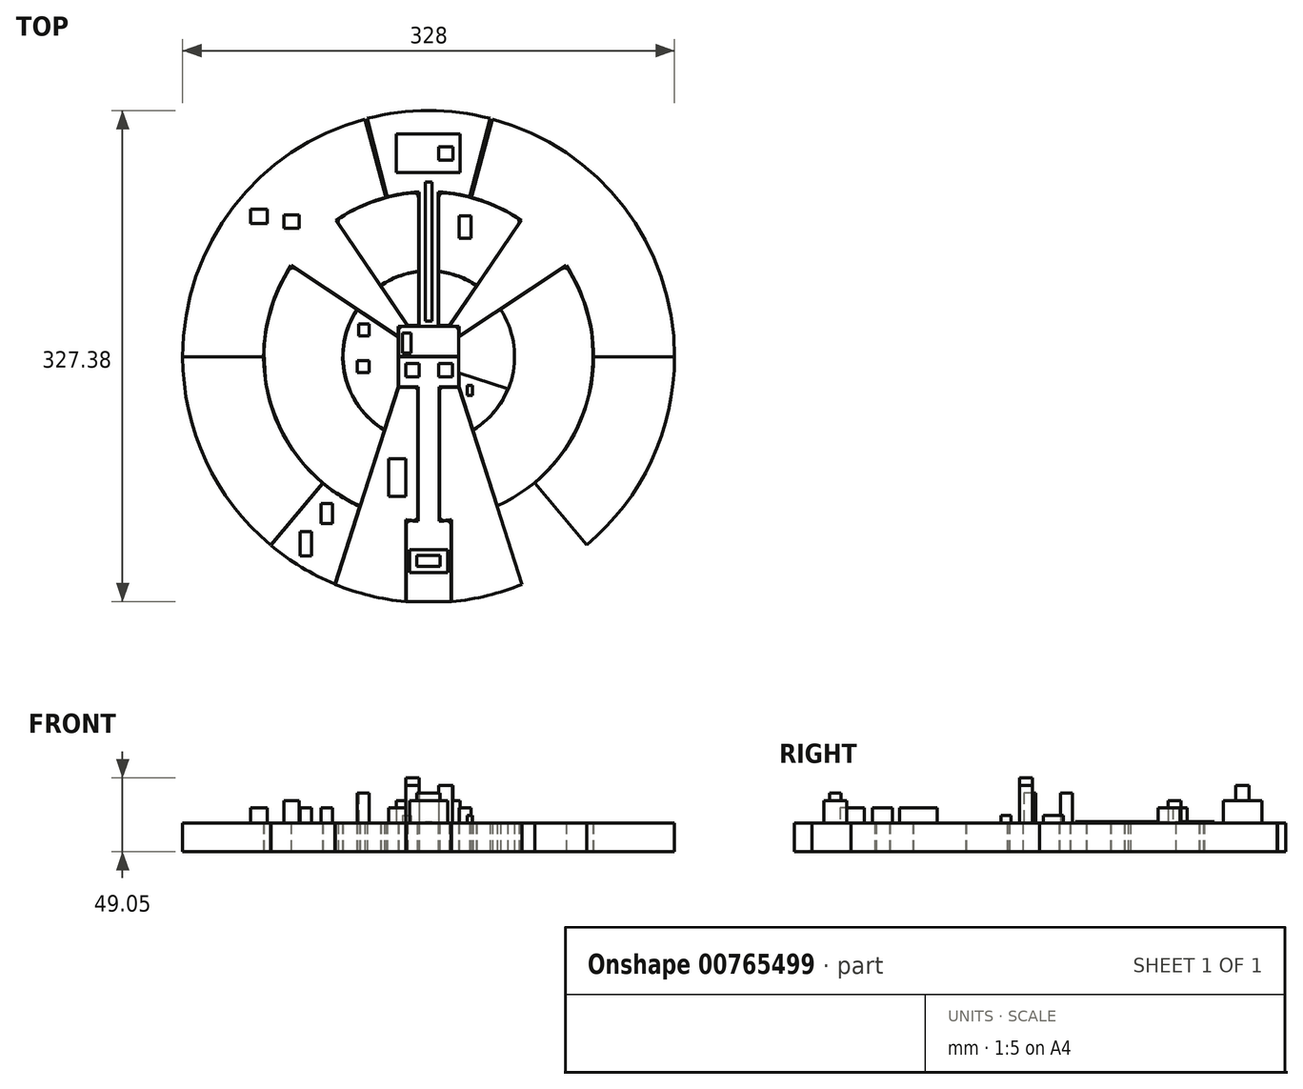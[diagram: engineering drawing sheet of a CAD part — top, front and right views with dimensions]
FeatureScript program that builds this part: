
annotation { "Feature Type Name" : "Feature", "Feature Type Description" : "" }
export const myFeature = defineFeature(function(context is Context, id is Id, definition is map)
    precondition{}
    {
        {
            var Q0;
            Q0=qCreatedBy(makeId("Top.planeOp"),FACE);
            var sketch = newSketch(context, id + "F0", { "sketchPlane" : qUnion([Q0])});
            skArc(sketch, "E0", {"start": v(-28.47, 106.25) * mm, "mid": v(-107.4, 23.8) * mm, "end": v(-70.7, -84.26) * mm});
            skCircle(sketch, "E1", {"center": v(0, 0) * mm, "radius": 57 * mm, "construction": true});
            skArc(sketch, "E2", {"start": v(-42.45, 158.41) * mm, "mid": v(-160.11, 35.5) * mm, "end": v(-105.42, -125.63) * mm});
            skLineSegment(sketch, "E3.trimOffspring", {"start": v(-28.47, 106.25) * mm, "end": v(-42.45, 158.41) * mm});
            skLineSegment(sketch, "E4.trimOffspring", {"start": v(28.47, 106.25) * mm, "end": v(42.45, 158.41) * mm});
            skLineSegment(sketch, "E5", {"start": v(70.7, -84.26) * mm, "end": v(105.42, -125.63) * mm});
            skLineSegment(sketch, "E6.trimOffspring", {"start": v(-70.7, -84.26) * mm, "end": v(-105.42, -125.63) * mm});
            skArc(sketch, "E7.trimOffspring", {"start": v(70.7, -84.26) * mm, "mid": v(107.4, 23.8) * mm, "end": v(28.47, 106.25) * mm});
            skArc(sketch, "E8.trimOffspring", {"start": v(105.42, -125.63) * mm, "mid": v(160.11, 35.5) * mm, "end": v(42.45, 158.41) * mm});
            skLineSegment(sketch, "E9", {"start": v(-164, 0) * mm, "end": v(-110, 0) * mm});
            skLineSegment(sketch, "E10.MirrorCS", {"start": v(164, 0) * mm, "end": v(110, 0) * mm});
            skSolve(sketch);
        }
        {
            var Q0;
            {var subQ0=sQuery(id+"F0.wireOp",EDGE,"E4.trimOffspring");Q0=makeQuery(id+"F0.imprint","IMPRINT",FACE,{"disambiguationData":[TD([[makeQuery(id+"F0.imprint","IMPRINT",EDGE,{"derivedFrom":subQ0}),-1.0]])]});}
            var Q1;
            {var subQ0=sQuery(id+"F0.wireOp",EDGE,"E3.trimOffspring");Q1=makeQuery(id+"F0.imprint","IMPRINT",FACE,{"disambiguationData":[TD([[makeQuery(id+"F0.imprint","IMPRINT",EDGE,{"derivedFrom":subQ0}),1.0]])]});}
            extrude(context, id + "F1", {"entities" : qUnion([Q0, Q1]), "depth" : 19.05 * mm, "offsetDistance" : 25 * mm});
        }
        {
            var Q0;
            Q0=qCreatedBy(makeId("Top.planeOp"),FACE);
            var sketch = newSketch(context, id + "F2", { "sketchPlane" : qUnion([Q0])});
            skLineSegment(sketch, "E11", {"start": v(13.85, 20.3) * mm, "end": v(61.98, 90.88) * mm});
            skCircle(sketch, "E12", {"center": v(0, 0) * mm, "radius": 110 * mm, "construction": true});
            skLineSegment(sketch, "E13", {"start": v(20.3, 13.46) * mm, "end": v(91.68, 60.79) * mm});
            skArc(sketch, "E14", {"start": v(61.98, 90.88) * mm, "mid": v(78.29, 77.27) * mm, "end": v(91.68, 60.79) * mm});
            skLineSegment(sketch, "E15.MirrorCS", {"start": v(-13.85, 20.3) * mm, "end": v(-61.98, 90.88) * mm});
            skLineSegment(sketch, "E16.MirrorCS", {"start": v(-20.3, 13.46) * mm, "end": v(-91.68, 60.79) * mm});
            skArc(sketch, "E17.MirrorCS", {"start": v(-61.98, 90.88) * mm, "mid": v(-78.29, 77.27) * mm, "end": v(-91.68, 60.79) * mm});
            skLineSegment(sketch, "E18", {"start": v(13.85, 20.3) * mm, "end": v(20.3, 20.3) * mm});
            skLineSegment(sketch, "E19", {"start": v(20.3, 20.3) * mm, "end": v(20.3, 13.46) * mm});
            skLineSegment(sketch, "E20", {"start": v(-13.85, 20.3) * mm, "end": v(-20.3, 20.3) * mm});
            skLineSegment(sketch, "E21", {"start": v(-20.3, 20.3) * mm, "end": v(-20.3, 13.46) * mm});
            skSolve(sketch);
        }
        {
            var Q0;
            Q0 = qSketchRegion(id + "F2", true);
            extrude(context, id + "F3", {"entities" : qUnion([Q0]), "operationType" : NewBodyOperationType.ADD, "depth" : 19.05 * mm, "offsetDistance" : 25 * mm});
        }
        {
            var Q0;
            Q0=qCreatedBy(makeId("Top.planeOp"),FACE);
            var sketch = newSketch(context, id + "F4", { "sketchPlane" : qUnion([Q0])});
            skLineSegment(sketch, "E22.top", {"start": v(-20, 20.31) * mm, "end": v(20, 20.31) * mm});
            skLineSegment(sketch, "E22.left", {"start": v(-20, 0.31) * mm, "end": v(-20, 20.31) * mm});
            skLineSegment(sketch, "E22.right", {"start": v(20, 0.31) * mm, "end": v(20, 20.31) * mm});
            skLineSegment(sketch, "E23", {"start": v(-20, 0.31) * mm, "end": v(20, 0.31) * mm});
            skSolve(sketch);
        }
        {
            var Q0;
            Q0 = qSketchRegion(id + "F4", true);
            var Q1;
            Q1=makeQuery(id+"F3.boolean.opBoolean","MERGE",FACE,{"derivedFrom":[makeQuery(id+"F1.opExtrude","CAP_FACE",FACE,{"disambiguationData":[OSD([sQuery(id+"F0.wireOp",EDGE,"E0"),sQuery(id+"F0.wireOp",EDGE,"E2"),sQuery(id+"F0.wireOp",EDGE,"E3.trimOffspring"),sQuery(id+"F0.wireOp",EDGE,"E6.trimOffspring")])],"isStart":false}),makeQuery(id+"F3.opExtrude","CAP_FACE",FACE,{"disambiguationData":[OSD([sQuery(id+"F2.wireOp",EDGE,"E15.MirrorCS"),sQuery(id+"F2.wireOp",EDGE,"E16.MirrorCS"),sQuery(id+"F2.wireOp",EDGE,"E17.MirrorCS")])],"isStart":false})]});
            extrude(context, id + "F5", {"entities" : qUnion([Q0]), "endBound" : BoundingType.UP_TO_SURFACE, "depth" : 25 * mm, "endBoundEntityFace" : qUnion([Q1]), "offsetDistance" : 25 * mm});
        }
        {
            var Q0;
            Q0=qCreatedBy(makeId("Top.planeOp"),FACE);
            var sketch = newSketch(context, id + "F6", { "sketchPlane" : qUnion([Q0])});
            skArc(sketch, "E24", {"start": v(27.47, 106.51) * mm, "mid": v(17.06, 108.67) * mm, "end": v(6.49, 109.8) * mm, "construction": true});
            skArc(sketch, "E25", {"start": v(27.47, 106.51) * mm, "mid": v(17.06, 108.67) * mm, "end": v(6.49, 109.8) * mm});
            skArc(sketch, "E26", {"start": v(40.96, 158.8) * mm, "mid": v(0, 164) * mm, "end": v(-40.96, 158.8) * mm});
            skLineSegment(sketch, "E27", {"start": v(-40.96, 158.8) * mm, "end": v(-27.47, 106.51) * mm});
            skLineSegment(sketch, "E28", {"start": v(40.96, 158.8) * mm, "end": v(27.47, 106.51) * mm});
            skArc(sketch, "E29", {"start": v(-27.47, 106.51) * mm, "mid": v(-17.06, 108.67) * mm, "end": v(-6.49, 109.8) * mm});
            skLineSegment(sketch, "E30.bottom", {"start": v(-6.49, 20.3) * mm, "end": v(6.49, 20.3) * mm});
            skLineSegment(sketch, "E30.left", {"start": v(-6.49, 20.3) * mm, "end": v(-6.49, 109.8) * mm});
            skLineSegment(sketch, "E30.right", {"start": v(6.49, 20.3) * mm, "end": v(6.49, 109.8) * mm});
            skArc(sketch, "E31.trimOffspring", {"start": v(-6.49, 109.8) * mm, "mid": v(-17.06, 108.67) * mm, "end": v(-27.47, 106.51) * mm, "construction": true});
            skArc(sketch, "E32.trimOffspring", {"start": v(6.49, 109.8) * mm, "mid": v(17.06, 108.67) * mm, "end": v(27.47, 106.51) * mm});
            skArc(sketch, "E33.trimOffspring", {"start": v(-6.49, 109.8) * mm, "mid": v(-17.06, 108.67) * mm, "end": v(-27.47, 106.51) * mm});
            skSolve(sketch);
        }
        {
            var Q0;
            Q0 = qSketchRegion(id + "F6", true);
            extrude(context, id + "F7", {"entities" : qUnion([Q0]), "depth" : 19.05 * mm, "offsetDistance" : 25 * mm});
        }
        {
            var Q0;
            Q0=qCreatedBy(makeId("Top.planeOp"),FACE);
            var sketch = newSketch(context, id + "F8", { "sketchPlane" : qUnion([Q0])});
            skArc(sketch, "E34", {"start": v(58.8, 92.6) * mm, "mid": v(35.53, 103.79) * mm, "end": v(10.29, 109.22) * mm});
            skLineSegment(sketch, "E35", {"start": v(-59.73, 88.1) * mm, "end": v(-32.04, 47.5) * mm});
            skLineSegment(sketch, "E36", {"start": v(-6.79, 56.9) * mm, "end": v(-6.79, 106.03) * mm});
            skLineSegment(sketch, "E37.MirrorCS", {"start": v(6.79, 56.9) * mm, "end": v(6.79, 106.03) * mm});
            skLineSegment(sketch, "E38.MirrorCS", {"start": v(59.73, 88.1) * mm, "end": v(32.04, 47.5) * mm});
            skArc(sketch, "E39.trimOffspring", {"start": v(-10.29, 109.22) * mm, "mid": v(-35.53, 103.79) * mm, "end": v(-58.8, 92.6) * mm});
            skArc(sketch, "E40", {"start": v(32.04, 47.5) * mm, "mid": v(19.97, 53.7) * mm, "end": v(6.79, 56.9) * mm});
            skArc(sketch, "E41.trimOffspring", {"start": v(-6.79, 56.9) * mm, "mid": v(-19.97, 53.7) * mm, "end": v(-32.04, 47.5) * mm});
            skPoint(sketch, "E42.visualSharp", {"position": v(-61.56, 90.8) * mm});
            skArc(sketch, "E42.filletArc", {"start": v(-58.8, 92.6) * mm, "mid": v(-60.22, 90.55) * mm, "end": v(-59.73, 88.1) * mm});
            skPoint(sketch, "E43.visualSharp", {"position": v(-6.79, 109.49) * mm});
            skArc(sketch, "E43.filletArc", {"start": v(-6.79, 106.03) * mm, "mid": v(-7.83, 108.4) * mm, "end": v(-10.29, 109.22) * mm});
            skPoint(sketch, "E44.visualSharp", {"position": v(6.79, 109.49) * mm});
            skArc(sketch, "E44.filletArc", {"start": v(10.29, 109.22) * mm, "mid": v(7.83, 108.4) * mm, "end": v(6.79, 106.03) * mm});
            skPoint(sketch, "E45.visualSharp", {"position": v(61.56, 90.8) * mm});
            skArc(sketch, "E45.filletArc", {"start": v(59.73, 88.1) * mm, "mid": v(60.22, 90.55) * mm, "end": v(58.8, 92.6) * mm});
            skSolve(sketch);
        }
        {
            var Q0;
            Q0 = qSketchRegion(id + "F8", true);
            extrude(context, id + "F9", {"entities" : qUnion([Q0]), "depth" : 19.05 * mm, "offsetDistance" : 25 * mm});
        }
        {
            var Q0;
            Q0=qCreatedBy(makeId("Top.planeOp"),FACE);
            var sketch = newSketch(context, id + "F10", { "sketchPlane" : qUnion([Q0])});
            skArc(sketch, "E46", {"start": v(31.87, 47.26) * mm, "mid": v(19.88, 53.42) * mm, "end": v(6.79, 56.6) * mm});
            skLineSegment(sketch, "E47", {"start": v(6.79, 20.77) * mm, "end": v(6.79, 56.6) * mm});
            skLineSegment(sketch, "E48", {"start": v(13.8, 20.77) * mm, "end": v(31.87, 47.26) * mm});
            skLineSegment(sketch, "E49", {"start": v(6.79, 20.77) * mm, "end": v(13.8, 20.77) * mm});
            skLineSegment(sketch, "E50.MirrorCS", {"start": v(-6.79, 20.77) * mm, "end": v(-6.79, 56.6) * mm});
            skLineSegment(sketch, "E51.MirrorCS", {"start": v(-13.8, 20.77) * mm, "end": v(-31.87, 47.26) * mm});
            skArc(sketch, "E52.MirrorCS", {"start": v(-31.87, 47.26) * mm, "mid": v(-19.88, 53.42) * mm, "end": v(-6.79, 56.6) * mm});
            skLineSegment(sketch, "E53.MirrorCS", {"start": v(-6.79, 20.77) * mm, "end": v(-13.8, 20.77) * mm});
            skSolve(sketch);
        }
        {
            var Q0;
            Q0=makeQuery(id+"F10.imprint","IMPRINT",FACE,{"disambiguationData":[TD([[makeQuery(id+"F10.imprint","IMPRINT",EDGE,{"derivedFrom":sQuery(id+"F10.wireOp",EDGE,"E50.MirrorCS")}),1.0]])]});
            var Q1;
            Q1=makeQuery(id+"F10.imprint","IMPRINT",FACE,{"disambiguationData":[TD([[makeQuery(id+"F10.imprint","IMPRINT",EDGE,{"derivedFrom":sQuery(id+"F10.wireOp",EDGE,"E46")}),1.0]])]});
            extrude(context, id + "F11", {"entities" : qUnion([Q0, Q1]), "depth" : 19.05 * mm, "offsetDistance" : 25 * mm});
        }
        {
            var Q0;
            Q0=qCreatedBy(makeId("Top.planeOp"),FACE);
            var sketch = newSketch(context, id + "F12", { "sketchPlane" : qUnion([Q0])});
            skLineSegment(sketch, "E54.bottom", {"start": v(-20, 0) * mm, "end": v(20, 0) * mm});
            skLineSegment(sketch, "E54.top", {"start": v(-20, -20) * mm, "end": v(-6.86, -20) * mm});
            skLineSegment(sketch, "E54.left", {"start": v(-20, 0) * mm, "end": v(-20, -20) * mm});
            skLineSegment(sketch, "E54.right", {"start": v(20, 0) * mm, "end": v(20, -20) * mm});
            skLineSegment(sketch, "E55.left", {"start": v(-6.86, -20) * mm, "end": v(-6.86, -109.79) * mm});
            skLineSegment(sketch, "E55.right", {"start": v(6.86, -20) * mm, "end": v(6.86, -109.79) * mm});
            skArc(sketch, "E56", {"start": v(-15, -108.97) * mm, "mid": v(-10.94, -109.45) * mm, "end": v(-6.86, -109.79) * mm});
            skLineSegment(sketch, "E57.top", {"start": v(-15, -163.31) * mm, "end": v(15, -163.31) * mm});
            skLineSegment(sketch, "E57.left", {"start": v(-15, -108.97) * mm, "end": v(-15, -163.31) * mm});
            skLineSegment(sketch, "E57.right", {"start": v(15, -108.97) * mm, "end": v(15, -163.31) * mm});
            skArc(sketch, "E58.trimOffspring", {"start": v(6.86, -109.79) * mm, "mid": v(10.94, -109.45) * mm, "end": v(15, -108.97) * mm});
            skLineSegment(sketch, "E59.trimOffspring", {"start": v(6.86, -20) * mm, "end": v(20, -20) * mm});
            skSolve(sketch);
        }
        {
            var Q0;
            Q0=makeQuery(id+"F12.imprint","IMPRINT",FACE,{"disambiguationData":[TD([[makeQuery(id+"F12.imprint","IMPRINT",EDGE,{"derivedFrom":sQuery(id+"F12.wireOp",EDGE,"E54.bottom")}),-1.0]])]});
            extrude(context, id + "F13", {"entities" : qUnion([Q0]), "depth" : 19.05 * mm, "offsetDistance" : 25 * mm});
        }
        {
            var Q0;
            Q0=qCreatedBy(makeId("Top.planeOp"),FACE);
            var sketch = newSketch(context, id + "F14", { "sketchPlane" : qUnion([Q0])});
            skLineSegment(sketch, "E60.bottom", {"start": v(0, 0) * mm, "end": v(-20, 0) * mm, "construction": true});
            skArc(sketch, "E61", {"start": v(-62.37, -151.78) * mm, "mid": v(-39.27, -159.32) * mm, "end": v(-15.31, -163.38) * mm});
            skLineSegment(sketch, "E62", {"start": v(-45.7, -100.2) * mm, "end": v(-62.37, -151.78) * mm});
            skLineSegment(sketch, "E63", {"start": v(-20.05, -20.3) * mm, "end": v(-45.7, -100.2) * mm});
            skLineSegment(sketch, "E64", {"start": v(-20.05, -20.3) * mm, "end": v(-7.16, -20.3) * mm});
            skLineSegment(sketch, "E65", {"start": v(-7.16, -20.3) * mm, "end": v(-7.16, -109.47) * mm});
            skPoint(sketch, "E66.end.orphan", {"position": v(-15.3, -108.93) * mm});
            skArc(sketch, "E67.trimOffspring", {"start": v(-15.31, -108.77) * mm, "mid": v(-11.24, -109.2) * mm, "end": v(-7.16, -109.47) * mm});
            skPoint(sketch, "E68.end.orphan", {"position": v(-15.31, -163.38) * mm});
            skLineSegment(sketch, "E69", {"start": v(-15.31, -108.77) * mm, "end": v(-15.31, -163.38) * mm});
            skPoint(sketch, "E70.MirrorCS.end.orphan", {"position": v(45.7, -100.2) * mm});
            skPoint(sketch, "E70.MirrorCS.start.orphan", {"position": v(20, -20) * mm});
            skPoint(sketch, "E71.MirrorCS.end.orphan", {"position": v(15.3, -108.93) * mm});
            skPoint(sketch, "E72.MirrorCS.end.orphan", {"position": v(62.37, -151.78) * mm});
            skPoint(sketch, "E73.MirrorCS.end.orphan", {"position": v(15.31, -163.38) * mm});
            skLineSegment(sketch, "E74.MirrorCS", {"start": v(7.16, -20.3) * mm, "end": v(7.16, -109.47) * mm});
            skArc(sketch, "E75.MirrorCS", {"start": v(15.31, -108.77) * mm, "mid": v(11.24, -109.2) * mm, "end": v(7.16, -109.47) * mm});
            skLineSegment(sketch, "E76.MirrorCS", {"start": v(15.31, -108.77) * mm, "end": v(15.31, -163.38) * mm});
            skArc(sketch, "E77.MirrorCS", {"start": v(62.37, -151.78) * mm, "mid": v(39.27, -159.32) * mm, "end": v(15.31, -163.38) * mm});
            skLineSegment(sketch, "E78.MirrorCS", {"start": v(45.7, -100.2) * mm, "end": v(62.37, -151.78) * mm});
            skLineSegment(sketch, "E79.MirrorCS", {"start": v(20.05, -20.3) * mm, "end": v(45.7, -100.2) * mm});
            skLineSegment(sketch, "E80.MirrorCS", {"start": v(20.05, -20.3) * mm, "end": v(7.16, -20.3) * mm});
            skSolve(sketch);
        }
        {
            var Q0;
            Q0=makeQuery(id+"F14.imprint","IMPRINT",FACE,{"disambiguationData":[TD([[makeQuery(id+"F14.imprint","IMPRINT",EDGE,{"derivedFrom":sQuery(id+"F14.wireOp",EDGE,"E61")}),1.0]])]});
            var Q1;
            Q1=makeQuery(id+"F14.imprint","IMPRINT",FACE,{"disambiguationData":[TD([[makeQuery(id+"F14.imprint","IMPRINT",EDGE,{"derivedFrom":sQuery(id+"F14.wireOp",EDGE,"E74.MirrorCS")}),1.0]])]});
            extrude(context, id + "F15", {"entities" : qUnion([Q0, Q1]), "depth" : 19.05 * mm, "offsetDistance" : 25 * mm});
        }
        {
            var Q0;
            Q0=qCreatedBy(makeId("Top.planeOp"),FACE);
            var sketch = newSketch(context, id + "F16", { "sketchPlane" : qUnion([Q0])});
            skArc(sketch, "E81", {"start": v(-105.19, -125.82) * mm, "mid": v(-84.88, -140.32) * mm, "end": v(-62.62, -151.57) * mm});
            skArc(sketch, "E82", {"start": v(-70.48, -84.46) * mm, "mid": v(-58.72, -93.02) * mm, "end": v(-45.94, -99.95) * mm});
            skLineSegment(sketch, "E83", {"start": v(-45.94, -99.95) * mm, "end": v(-62.62, -151.57) * mm});
            skLineSegment(sketch, "E84", {"start": v(-70.48, -84.46) * mm, "end": v(-105.19, -125.82) * mm});
            skArc(sketch, "E85.MirrorCS", {"start": v(70.48, -84.46) * mm, "mid": v(58.72, -93.02) * mm, "end": v(45.94, -99.95) * mm});
            skLineSegment(sketch, "E86.MirrorCS", {"start": v(70.48, -84.46) * mm, "end": v(105.19, -125.82) * mm});
            skLineSegment(sketch, "E87.MirrorCS", {"start": v(45.94, -99.95) * mm, "end": v(62.62, -151.57) * mm});
            skArc(sketch, "E88.MirrorCS", {"start": v(105.19, -125.82) * mm, "mid": v(84.88, -140.32) * mm, "end": v(62.62, -151.57) * mm});
            skSolve(sketch);
        }
        {
            var Q0;
            Q0=makeQuery(id+"F16.imprint","IMPRINT",FACE,{"disambiguationData":[TD([[makeQuery(id+"F16.imprint","IMPRINT",EDGE,{"derivedFrom":sQuery(id+"F16.wireOp",EDGE,"E81")}),1.0]])]});
            var Q1;
            Q1=makeQuery(id+"F16.imprint","IMPRINT",FACE,{"disambiguationData":[TD([[makeQuery(id+"F16.imprint","IMPRINT",EDGE,{"derivedFrom":sQuery(id+"F16.wireOp",EDGE,"E85.MirrorCS")}),1.0]])]});
            extrude(context, id + "F17", {"entities" : qUnion([Q0, Q1]), "depth" : 19.05 * mm, "offsetDistance" : 25 * mm});
        }
        {
            var Q0;
            Q0=qCreatedBy(makeId("Top.planeOp"),FACE);
            var sketch = newSketch(context, id + "F18", { "sketchPlane" : qUnion([Q0])});
            skArc(sketch, "E89", {"start": v(-47.67, 31.25) * mm, "mid": v(-55.59, -12.62) * mm, "end": v(-29.5, -48.77) * mm});
            skLineSegment(sketch, "E90", {"start": v(-20.3, 13.1) * mm, "end": v(-20.3, -20.1) * mm});
            skLineSegment(sketch, "E91", {"start": v(-47.67, 31.25) * mm, "end": v(-20.3, 13.1) * mm});
            skLineSegment(sketch, "E92", {"start": v(-20.3, -20.1) * mm, "end": v(-29.5, -48.77) * mm});
            skArc(sketch, "E93.MirrorCS", {"start": v(47.67, 31.25) * mm, "mid": v(56.72, 5.65) * mm, "end": v(52.9, -21.24) * mm});
            skLineSegment(sketch, "E94.MirrorCS", {"start": v(20.3, -20.1) * mm, "end": v(29.5, -48.77) * mm});
            skLineSegment(sketch, "E95.MirrorCS", {"start": v(20.3, 13.1) * mm, "end": v(20.3, -10.69) * mm});
            skLineSegment(sketch, "E96.MirrorCS", {"start": v(47.67, 31.25) * mm, "end": v(20.3, 13.1) * mm});
            skLineSegment(sketch, "E97", {"start": v(20.3, -11) * mm, "end": v(52.78, -21.52) * mm});
            skLineSegment(sketch, "E98.0", {"start": v(20.3, -10.69) * mm, "end": v(52.9, -21.24) * mm});
            skArc(sketch, "E99.trimOffspring", {"start": v(52.78, -21.52) * mm, "mid": v(43.34, -37.02) * mm, "end": v(29.5, -48.77) * mm});
            skPoint(sketch, "E100.MirrorCS.start.orphan", {"position": v(47.67, 31.25) * mm});
            skPoint(sketch, "E101.trimOffspring.end.orphan", {"position": v(29.5, -48.77) * mm});
            skLineSegment(sketch, "E102.trimOffspring", {"start": v(20.3, -11) * mm, "end": v(20.3, -20.1) * mm});
            skSolve(sketch);
        }
        {
            var Q0;
            Q0=makeQuery(id+"F18.imprint","IMPRINT",FACE,{"disambiguationData":[TD([[makeQuery(id+"F18.imprint","IMPRINT",EDGE,{"derivedFrom":sQuery(id+"F18.wireOp",EDGE,"E89")}),1.0]])]});
            var Q1;
            Q1=makeQuery(id+"F18.imprint","IMPRINT",FACE,{"disambiguationData":[TD([[makeQuery(id+"F18.imprint","IMPRINT",EDGE,{"derivedFrom":sQuery(id+"F18.wireOp",EDGE,"E93.MirrorCS")}),-1.0]])]});
            var Q2;
            Q2=makeQuery(id+"F18.imprint","IMPRINT",FACE,{"disambiguationData":[TD([[makeQuery(id+"F18.imprint","IMPRINT",EDGE,{"derivedFrom":sQuery(id+"F18.wireOp",EDGE,"E94.MirrorCS")}),1.0]])]});
            extrude(context, id + "F19", {"entities" : qUnion([Q0, Q1, Q2]), "depth" : 19.05 * mm, "offsetDistance" : 25 * mm});
        }
        {
            var Q0;
            Q0=qCreatedBy(makeId("Top.planeOp"),FACE);
            var sketch = newSketch(context, id + "F20", { "sketchPlane" : qUnion([Q0])});
            skArc(sketch, "E103", {"start": v(-91.6, 60.37) * mm, "mid": v(-105.48, -30.15) * mm, "end": v(-45.85, -99.66) * mm});
            skArc(sketch, "E104", {"start": v(-47.92, 31.42) * mm, "mid": v(-55.87, -12.72) * mm, "end": v(-29.6, -49.06) * mm});
            skLineSegment(sketch, "E105", {"start": v(-29.6, -49.06) * mm, "end": v(-45.85, -99.66) * mm});
            skLineSegment(sketch, "E106", {"start": v(-91.6, 60.37) * mm, "end": v(-47.92, 31.42) * mm});
            skLineSegment(sketch, "E107.MirrorCS", {"start": v(91.6, 60.37) * mm, "end": v(47.92, 31.42) * mm});
            skArc(sketch, "E108.MirrorCS", {"start": v(47.92, 31.42) * mm, "mid": v(55.87, -12.72) * mm, "end": v(29.6, -49.06) * mm});
            skLineSegment(sketch, "E109.MirrorCS", {"start": v(29.6, -49.06) * mm, "end": v(45.85, -99.66) * mm});
            skArc(sketch, "E110.MirrorCS", {"start": v(91.6, 60.37) * mm, "mid": v(105.48, -30.15) * mm, "end": v(45.85, -99.66) * mm});
            skSolve(sketch);
        }
        {
            var Q0;
            Q0=makeQuery(id+"F20.imprint","IMPRINT",FACE,{"disambiguationData":[TD([[makeQuery(id+"F20.imprint","IMPRINT",EDGE,{"derivedFrom":sQuery(id+"F20.wireOp",EDGE,"E103")}),1.0]])]});
            var Q1;
            Q1=makeQuery(id+"F20.imprint","IMPRINT",FACE,{"disambiguationData":[TD([[makeQuery(id+"F20.imprint","IMPRINT",EDGE,{"derivedFrom":sQuery(id+"F20.wireOp",EDGE,"E107.MirrorCS")}),1.0]])]});
            extrude(context, id + "F21", {"entities" : qUnion([Q0, Q1]), "depth" : 19.05 * mm, "offsetDistance" : 25 * mm});
        }
        {
            var Q0;
            {var subQ0=sQuery(id+"F0.wireOp",EDGE,"E6.trimOffspring");Q0=makeQuery(id+"F0.imprint","IMPRINT",FACE,{"disambiguationData":[TD([[makeQuery(id+"F0.imprint","IMPRINT",EDGE,{"derivedFrom":subQ0}),-1.0]])]});}
            var Q1;
            {var subQ0=sQuery(id+"F0.wireOp",EDGE,"E5");Q1=makeQuery(id+"F0.imprint","IMPRINT",FACE,{"disambiguationData":[TD([[makeQuery(id+"F0.imprint","IMPRINT",EDGE,{"derivedFrom":subQ0}),1.0]])]});}
            extrude(context, id + "F22", {"entities" : qUnion([Q0, Q1]), "depth" : 19.05 * mm, "offsetDistance" : 25 * mm});
        }
        {
            var Q0;
            Q0=makeQuery(id+"F7.opExtrude","CAP_FACE",FACE,{"disambiguationData":[OSD([sQuery(id+"F6.wireOp",EDGE,"E26"),sQuery(id+"F6.wireOp",EDGE,"E27"),sQuery(id+"F6.wireOp",EDGE,"E28"),sQuery(id+"F6.wireOp",EDGE,"E30.bottom"),sQuery(id+"F6.wireOp",EDGE,"E30.left"),sQuery(id+"F6.wireOp",EDGE,"E30.right"),sQuery(id+"F6.wireOp",EDGE,"E32.trimOffspring"),sQuery(id+"F6.wireOp",EDGE,"E33.trimOffspring")])],"isStart":false});
            var sketch = newSketch(context, id + "F23", { "sketchPlane" : qUnion([Q0])});
            skLineSegment(sketch, "E111.bottom", {"start": v(-21.62, 148.38) * mm, "end": v(21.07, 148.38) * mm});
            skLineSegment(sketch, "E111.top", {"start": v(-21.62, 122.64) * mm, "end": v(21.07, 122.64) * mm});
            skLineSegment(sketch, "E111.left", {"start": v(-21.62, 148.38) * mm, "end": v(-21.62, 122.64) * mm});
            skLineSegment(sketch, "E111.right", {"start": v(21.07, 148.38) * mm, "end": v(21.07, 122.64) * mm});
            skSolve(sketch);
        }
        {
            var Q0;
            Q0=makeQuery(id+"F23.imprint","IMPRINT",FACE,{"disambiguationData":[TD([[makeQuery(id+"F23.imprint","IMPRINT",EDGE,{"derivedFrom":sQuery(id+"F23.wireOp",EDGE,"E111.bottom")}),-1.0]])]});
            extrude(context, id + "F24", {"entities" : qUnion([Q0]), "depth" : 15 * mm, "offsetDistance" : 25 * mm});
        }
        {
            var Q0;
            Q0=makeQuery(id+"F24.opExtrude","CAP_FACE",FACE,{"disambiguationData":[OSD([sQuery(id+"F23.wireOp",EDGE,"E111.bottom"),sQuery(id+"F23.wireOp",EDGE,"E111.top"),sQuery(id+"F23.wireOp",EDGE,"E111.left"),sQuery(id+"F23.wireOp",EDGE,"E111.right")])],"isStart":false});
            var sketch = newSketch(context, id + "F25", { "sketchPlane" : qUnion([Q0])});
            skLineSegment(sketch, "E112.bottom", {"start": v(6.6, 139.76) * mm, "end": v(16.3, 139.76) * mm});
            skLineSegment(sketch, "E112.top", {"start": v(6.6, 130.95) * mm, "end": v(16.3, 130.95) * mm});
            skLineSegment(sketch, "E112.left", {"start": v(6.6, 139.76) * mm, "end": v(6.6, 130.95) * mm});
            skLineSegment(sketch, "E112.right", {"start": v(16.3, 139.76) * mm, "end": v(16.3, 130.95) * mm});
            skSolve(sketch);
        }
        {
            var Q0;
            Q0=makeQuery(id+"F25.imprint","IMPRINT",FACE,{"disambiguationData":[TD([[makeQuery(id+"F25.imprint","IMPRINT",EDGE,{"derivedFrom":sQuery(id+"F25.wireOp",EDGE,"E112.bottom")}),-1.0]])]});
            extrude(context, id + "F26", {"entities" : qUnion([Q0]), "operationType" : NewBodyOperationType.ADD, "depth" : 10 * mm, "offsetDistance" : 25 * mm});
        }
        {
            var Q0;
            Q0=makeQuery(id+"F13.opExtrude","CAP_FACE",FACE,{"disambiguationData":[OSD([sQuery(id+"F12.wireOp",EDGE,"E54.bottom"),sQuery(id+"F12.wireOp",EDGE,"E54.top"),sQuery(id+"F12.wireOp",EDGE,"E54.left"),sQuery(id+"F12.wireOp",EDGE,"E54.right"),sQuery(id+"F12.wireOp",EDGE,"E55.left"),sQuery(id+"F12.wireOp",EDGE,"E55.right"),sQuery(id+"F12.wireOp",EDGE,"E56"),sQuery(id+"F12.wireOp",EDGE,"E57.top"),sQuery(id+"F12.wireOp",EDGE,"E57.left"),sQuery(id+"F12.wireOp",EDGE,"E57.right"),sQuery(id+"F12.wireOp",EDGE,"E58.trimOffspring"),sQuery(id+"F12.wireOp",EDGE,"E59.trimOffspring")])],"isStart":false});
            var sketch = newSketch(context, id + "F27", { "sketchPlane" : qUnion([Q0])});
            skLineSegment(sketch, "E113.bottom", {"start": v(-15.12, -4.7) * mm, "end": v(-6.46, -4.7) * mm});
            skLineSegment(sketch, "E113.top", {"start": v(-15.12, -13.37) * mm, "end": v(-6.46, -13.37) * mm});
            skLineSegment(sketch, "E113.left", {"start": v(-15.12, -4.7) * mm, "end": v(-15.12, -13.37) * mm});
            skLineSegment(sketch, "E113.right", {"start": v(-6.46, -4.7) * mm, "end": v(-6.46, -13.37) * mm});
            skLineSegment(sketch, "E114.bottom", {"start": v(6.54, -4.7) * mm, "end": v(15.82, -4.7) * mm});
            skLineSegment(sketch, "E114.top", {"start": v(6.54, -13.37) * mm, "end": v(15.82, -13.37) * mm});
            skLineSegment(sketch, "E114.left", {"start": v(6.54, -4.7) * mm, "end": v(6.54, -13.37) * mm});
            skLineSegment(sketch, "E114.right", {"start": v(15.82, -4.7) * mm, "end": v(15.82, -13.37) * mm});
            skSolve(sketch);
        }
        {
            var Q0;
            Q0=makeQuery(id+"F27.imprint","IMPRINT",FACE,{"disambiguationData":[TD([[makeQuery(id+"F27.imprint","IMPRINT",EDGE,{"derivedFrom":sQuery(id+"F27.wireOp",EDGE,"E113.bottom")}),-1.0]])]});
            extrude(context, id + "F28", {"entities" : qUnion([Q0]), "depth" : 30 * mm, "offsetDistance" : 25 * mm});
        }
        {
            var Q0;
            Q0 = qSketchRegion(id + "F27", true);
            extrude(context, id + "F29", {"entities" : qUnion([Q0]), "depth" : 25 * mm, "offsetDistance" : 25 * mm});
        }
        {
            var Q0;
            Q0=makeQuery(id+"F3.boolean.opBoolean","MERGE",FACE,{"derivedFrom":[makeQuery(id+"F1.opExtrude","CAP_FACE",FACE,{"disambiguationData":[OSD([sQuery(id+"F0.wireOp",EDGE,"E0"),sQuery(id+"F0.wireOp",EDGE,"E2"),sQuery(id+"F0.wireOp",EDGE,"E3.trimOffspring"),sQuery(id+"F0.wireOp",EDGE,"E9")])],"isStart":false}),makeQuery(id+"F3.opExtrude","CAP_FACE",FACE,{"disambiguationData":[OSD([sQuery(id+"F2.wireOp",EDGE,"E15.MirrorCS"),sQuery(id+"F2.wireOp",EDGE,"E16.MirrorCS"),sQuery(id+"F2.wireOp",EDGE,"E17.MirrorCS"),sQuery(id+"F2.wireOp",EDGE,"E20"),sQuery(id+"F2.wireOp",EDGE,"E21")])],"isStart":false})]});
            var sketch = newSketch(context, id + "F30", { "sketchPlane" : qUnion([Q0])});
            skLineSegment(sketch, "E115.bottom", {"start": v(-118.62, 98.32) * mm, "end": v(-107.66, 98.32) * mm});
            skLineSegment(sketch, "E115.top", {"start": v(-118.62, 88.85) * mm, "end": v(-107.66, 88.85) * mm});
            skLineSegment(sketch, "E115.left", {"start": v(-118.62, 98.32) * mm, "end": v(-118.62, 88.85) * mm});
            skLineSegment(sketch, "E115.right", {"start": v(-107.66, 98.32) * mm, "end": v(-107.66, 88.85) * mm});
            skPoint(sketch, "E116.oppositeSnap0", {"position": v(-113.14, 88.85) * mm});
            skLineSegment(sketch, "E116.bottom", {"start": v(-107.66, 93.58) * mm, "end": v(-102.42, 93.58) * mm});
            skLineSegment(sketch, "E116.top", {"start": v(-107.66, 88.85) * mm, "end": v(-102.42, 88.85) * mm});
            skLineSegment(sketch, "E116.left", {"start": v(-107.66, 93.58) * mm, "end": v(-107.66, 88.85) * mm});
            skLineSegment(sketch, "E116.right", {"start": v(-102.42, 93.58) * mm, "end": v(-102.42, 88.85) * mm});
            skSolve(sketch);
        }
        {
            var Q0;
            Q0=makeQuery(id+"F30.imprint","IMPRINT",FACE,{"disambiguationData":[TD([[makeQuery(id+"F30.imprint","IMPRINT",EDGE,{"derivedFrom":sQuery(id+"F30.wireOp",EDGE,"E115.bottom")}),-1.0]])]});
            extrude(context, id + "F31", {"entities" : qUnion([Q0]), "depth" : 10 * mm, "offsetDistance" : 25 * mm});
        }
        {
            var Q0;
            Q0=makeQuery(id+"F3.boolean.opBoolean","MERGE",FACE,{"derivedFrom":[makeQuery(id+"F1.opExtrude","CAP_FACE",FACE,{"disambiguationData":[OSD([sQuery(id+"F0.wireOp",EDGE,"E0"),sQuery(id+"F0.wireOp",EDGE,"E2"),sQuery(id+"F0.wireOp",EDGE,"E3.trimOffspring"),sQuery(id+"F0.wireOp",EDGE,"E9")])],"isStart":false}),makeQuery(id+"F3.opExtrude","CAP_FACE",FACE,{"disambiguationData":[OSD([sQuery(id+"F2.wireOp",EDGE,"E15.MirrorCS"),sQuery(id+"F2.wireOp",EDGE,"E16.MirrorCS"),sQuery(id+"F2.wireOp",EDGE,"E17.MirrorCS"),sQuery(id+"F2.wireOp",EDGE,"E20"),sQuery(id+"F2.wireOp",EDGE,"E21")])],"isStart":false})]});
            var sketch = newSketch(context, id + "F32", { "sketchPlane" : qUnion([Q0])});
            skLineSegment(sketch, "E117.bottom", {"start": v(-96.45, 94.4) * mm, "end": v(-86.26, 94.4) * mm});
            skLineSegment(sketch, "E117.top", {"start": v(-96.45, 85.74) * mm, "end": v(-86.26, 85.74) * mm});
            skLineSegment(sketch, "E117.left", {"start": v(-96.45, 94.4) * mm, "end": v(-96.45, 85.74) * mm});
            skLineSegment(sketch, "E117.right", {"start": v(-86.26, 94.4) * mm, "end": v(-86.26, 85.74) * mm});
            skSolve(sketch);
        }
        {
            var Q0;
            Q0=makeQuery(id+"F32.imprint","IMPRINT",FACE,{"disambiguationData":[TD([[makeQuery(id+"F32.imprint","IMPRINT",EDGE,{"derivedFrom":sQuery(id+"F32.wireOp",EDGE,"E117.bottom")}),-1.0]])]});
            extrude(context, id + "F33", {"entities" : qUnion([Q0]), "depth" : 15 * mm, "offsetDistance" : 25 * mm});
        }
        {
            var Q0;
            Q0=makeQuery(id+"F15.opExtrude","CAP_FACE",FACE,{"disambiguationData":[OSD([sQuery(id+"F14.wireOp",EDGE,"E61"),sQuery(id+"F14.wireOp",EDGE,"E62"),sQuery(id+"F14.wireOp",EDGE,"E63"),sQuery(id+"F14.wireOp",EDGE,"E64"),sQuery(id+"F14.wireOp",EDGE,"E65"),sQuery(id+"F14.wireOp",EDGE,"E67.trimOffspring"),sQuery(id+"F14.wireOp",EDGE,"E69")])],"isStart":false});
            var sketch = newSketch(context, id + "F34", { "sketchPlane" : qUnion([Q0])});
            skLineSegment(sketch, "E118.bottom", {"start": v(-26.5, -68.17) * mm, "end": v(-15.31, -68.17) * mm});
            skLineSegment(sketch, "E118.top", {"start": v(-26.5, -93.24) * mm, "end": v(-15.31, -93.24) * mm});
            skLineSegment(sketch, "E118.left", {"start": v(-26.5, -68.17) * mm, "end": v(-26.5, -93.24) * mm});
            skLineSegment(sketch, "E118.right", {"start": v(-15.31, -68.17) * mm, "end": v(-15.31, -93.24) * mm});
            skSolve(sketch);
        }
        {
            var Q0;
            Q0 = qSketchRegion(id + "F34", true);
            extrude(context, id + "F35", {"entities" : qUnion([Q0]), "depth" : 10 * mm, "offsetDistance" : 25 * mm});
        }
        {
            var Q0;
            Q0=makeQuery(id+"F13.opExtrude","CAP_FACE",FACE,{"disambiguationData":[OSD([sQuery(id+"F12.wireOp",EDGE,"E54.bottom"),sQuery(id+"F12.wireOp",EDGE,"E54.top"),sQuery(id+"F12.wireOp",EDGE,"E54.left"),sQuery(id+"F12.wireOp",EDGE,"E54.right"),sQuery(id+"F12.wireOp",EDGE,"E55.left"),sQuery(id+"F12.wireOp",EDGE,"E55.right"),sQuery(id+"F12.wireOp",EDGE,"E56"),sQuery(id+"F12.wireOp",EDGE,"E57.top"),sQuery(id+"F12.wireOp",EDGE,"E57.left"),sQuery(id+"F12.wireOp",EDGE,"E57.right"),sQuery(id+"F12.wireOp",EDGE,"E58.trimOffspring"),sQuery(id+"F12.wireOp",EDGE,"E59.trimOffspring")])],"isStart":false});
            var sketch = newSketch(context, id + "F36", { "sketchPlane" : qUnion([Q0])});
            skLineSegment(sketch, "E119.bottom", {"start": v(-12.75, -128.56) * mm, "end": v(12.75, -128.56) * mm});
            skLineSegment(sketch, "E119.top", {"start": v(-12.75, -143.9) * mm, "end": v(12.75, -143.9) * mm});
            skLineSegment(sketch, "E119.left", {"start": v(-12.75, -128.56) * mm, "end": v(-12.75, -143.9) * mm});
            skLineSegment(sketch, "E119.right", {"start": v(12.75, -128.56) * mm, "end": v(12.75, -143.9) * mm});
            skSolve(sketch);
        }
        {
            var Q0;
            Q0=makeQuery(id+"F36.imprint","IMPRINT",FACE,{"disambiguationData":[TD([[makeQuery(id+"F36.imprint","IMPRINT",EDGE,{"derivedFrom":sQuery(id+"F36.wireOp",EDGE,"E119.bottom")}),-1.0]])]});
            extrude(context, id + "F37", {"entities" : qUnion([Q0]), "depth" : 15 * mm, "offsetDistance" : 25 * mm});
        }
        {
            var Q0;
            Q0=makeQuery(id+"F37.opExtrude","CAP_FACE",FACE,{"disambiguationData":[OSD([sQuery(id+"F36.wireOp",EDGE,"E119.bottom"),sQuery(id+"F36.wireOp",EDGE,"E119.top"),sQuery(id+"F36.wireOp",EDGE,"E119.left"),sQuery(id+"F36.wireOp",EDGE,"E119.right")])],"isStart":false});
            var sketch = newSketch(context, id + "F38", { "sketchPlane" : qUnion([Q0])});
            skLineSegment(sketch, "E120.bottom", {"start": v(-7.75, -132.56) * mm, "end": v(7.75, -132.56) * mm});
            skLineSegment(sketch, "E120.top", {"start": v(-7.75, -139.9) * mm, "end": v(7.75, -139.9) * mm});
            skLineSegment(sketch, "E120.left", {"start": v(-7.75, -132.56) * mm, "end": v(-7.75, -139.9) * mm});
            skLineSegment(sketch, "E120.right", {"start": v(7.75, -132.56) * mm, "end": v(7.75, -139.9) * mm});
            skSolve(sketch);
        }
        {
            var Q0;
            Q0 = qSketchRegion(id + "F38", true);
            extrude(context, id + "F39", {"entities" : qUnion([Q0]), "operationType" : NewBodyOperationType.ADD, "depth" : 5 * mm, "offsetDistance" : 25 * mm});
        }
        {
            var Q0;
            Q0=makeQuery(id+"F17.opExtrude","CAP_FACE",FACE,{"disambiguationData":[OSD([sQuery(id+"F16.wireOp",EDGE,"E81"),sQuery(id+"F16.wireOp",EDGE,"E82"),sQuery(id+"F16.wireOp",EDGE,"E83"),sQuery(id+"F16.wireOp",EDGE,"E84")])],"isStart":false});
            var sketch = newSketch(context, id + "F40", { "sketchPlane" : qUnion([Q0])});
            skLineSegment(sketch, "E121.bottom", {"start": v(-71.82, -97.96) * mm, "end": v(-64.13, -97.96) * mm});
            skLineSegment(sketch, "E121.top", {"start": v(-71.82, -111.4) * mm, "end": v(-64.13, -111.4) * mm});
            skLineSegment(sketch, "E121.left", {"start": v(-71.82, -97.96) * mm, "end": v(-71.82, -111.4) * mm});
            skLineSegment(sketch, "E121.right", {"start": v(-64.13, -97.96) * mm, "end": v(-64.13, -111.4) * mm});
            skLineSegment(sketch, "E122.bottom", {"start": v(-85.65, -116.79) * mm, "end": v(-77.97, -116.79) * mm});
            skLineSegment(sketch, "E122.top", {"start": v(-85.65, -132.93) * mm, "end": v(-77.97, -132.93) * mm});
            skLineSegment(sketch, "E122.left", {"start": v(-85.65, -116.79) * mm, "end": v(-85.65, -132.93) * mm});
            skLineSegment(sketch, "E122.right", {"start": v(-77.97, -116.79) * mm, "end": v(-77.97, -132.93) * mm});
            skSolve(sketch);
        }
        {
            var Q0;
            Q0 = qSketchRegion(id + "F40", true);
            extrude(context, id + "F41", {"entities" : qUnion([Q0]), "depth" : 10 * mm, "offsetDistance" : 25 * mm});
        }
        {
            var Q0;
            Q0=makeQuery(id+"F19.opExtrude","CAP_FACE",FACE,{"disambiguationData":[OSD([sQuery(id+"F18.wireOp",EDGE,"E89"),sQuery(id+"F18.wireOp",EDGE,"E90"),sQuery(id+"F18.wireOp",EDGE,"E91"),sQuery(id+"F18.wireOp",EDGE,"E92")])],"isStart":false});
            var sketch = newSketch(context, id + "F42", { "sketchPlane" : qUnion([Q0])});
            skLineSegment(sketch, "E123.bottom", {"start": v(-46.62, 21.91) * mm, "end": v(-39.64, 21.91) * mm});
            skLineSegment(sketch, "E123.top", {"start": v(-46.62, 13.94) * mm, "end": v(-39.64, 13.94) * mm});
            skLineSegment(sketch, "E123.left", {"start": v(-46.62, 21.91) * mm, "end": v(-46.62, 13.94) * mm});
            skLineSegment(sketch, "E123.right", {"start": v(-39.64, 21.91) * mm, "end": v(-39.64, 13.94) * mm});
            skLineSegment(sketch, "E124.bottom", {"start": v(-47.67, -2.5) * mm, "end": v(-39.64, -2.5) * mm});
            skLineSegment(sketch, "E124.top", {"start": v(-47.67, -10.48) * mm, "end": v(-39.64, -10.48) * mm});
            skLineSegment(sketch, "E124.left", {"start": v(-47.67, -2.5) * mm, "end": v(-47.67, -10.48) * mm});
            skLineSegment(sketch, "E124.right", {"start": v(-39.64, -2.5) * mm, "end": v(-39.64, -10.48) * mm});
            skSolve(sketch);
        }
        {
            var Q0;
            Q0 = qSketchRegion(id + "F42", true);
            extrude(context, id + "F43", {"entities" : qUnion([Q0]), "depth" : 20 * mm, "offsetDistance" : 25 * mm});
        }
        {
            var Q0;
            Q0=makeQuery(id+"F19.opExtrude","CAP_FACE",FACE,{"disambiguationData":[OSD([sQuery(id+"F18.wireOp",EDGE,"E94.MirrorCS"),sQuery(id+"F18.wireOp",EDGE,"E97"),sQuery(id+"F18.wireOp",EDGE,"E99.trimOffspring"),sQuery(id+"F18.wireOp",EDGE,"E102.trimOffspring")])],"isStart":false});
            var sketch = newSketch(context, id + "F44", { "sketchPlane" : qUnion([Q0])});
            skLineSegment(sketch, "E125.bottom", {"start": v(25.68, -19.07) * mm, "end": v(29.35, -19.07) * mm});
            skLineSegment(sketch, "E125.top", {"start": v(25.68, -25.73) * mm, "end": v(29.35, -25.73) * mm});
            skLineSegment(sketch, "E125.left", {"start": v(25.68, -19.07) * mm, "end": v(25.68, -25.73) * mm});
            skLineSegment(sketch, "E125.right", {"start": v(29.35, -19.07) * mm, "end": v(29.35, -25.73) * mm});
            skSolve(sketch);
        }
        {
            var Q0;
            Q0 = qSketchRegion(id + "F44", true);
            extrude(context, id + "F45", {"entities" : qUnion([Q0]), "depth" : 5 * mm, "offsetDistance" : 25 * mm});
        }
        {
            var Q0;
            Q0=makeQuery(id+"F5.opExtrude","CAP_FACE",FACE,{"disambiguationData":[OSD([sQuery(id+"F4.wireOp",EDGE,"E22.top"),sQuery(id+"F4.wireOp",EDGE,"E22.left"),sQuery(id+"F4.wireOp",EDGE,"E22.right"),sQuery(id+"F4.wireOp",EDGE,"E23")])],"isStart":false});
            var sketch = newSketch(context, id + "F46", { "sketchPlane" : qUnion([Q0])});
            skLineSegment(sketch, "E126.bottom", {"start": v(-17.48, 15.82) * mm, "end": v(-11.84, 15.82) * mm});
            skLineSegment(sketch, "E126.top", {"start": v(-17.48, 2.49) * mm, "end": v(-11.84, 2.49) * mm});
            skLineSegment(sketch, "E126.left", {"start": v(-17.48, 15.82) * mm, "end": v(-17.48, 2.49) * mm});
            skLineSegment(sketch, "E126.right", {"start": v(-11.84, 15.82) * mm, "end": v(-11.84, 2.49) * mm});
            skSolve(sketch);
        }
        {
            var Q0;
            Q0=makeQuery(id+"F46.imprint","IMPRINT",FACE,{"disambiguationData":[TD([[makeQuery(id+"F46.imprint","IMPRINT",EDGE,{"derivedFrom":sQuery(id+"F46.wireOp",EDGE,"E126.bottom")}),-1.0]])]});
            extrude(context, id + "F47", {"entities" : qUnion([Q0]), "depth" : 5 * mm, "offsetDistance" : 25 * mm});
        }
        {
            var Q0;
            Q0=makeQuery(id+"F7.opExtrude","CAP_FACE",FACE,{"disambiguationData":[OSD([sQuery(id+"F6.wireOp",EDGE,"E26"),sQuery(id+"F6.wireOp",EDGE,"E27"),sQuery(id+"F6.wireOp",EDGE,"E28"),sQuery(id+"F6.wireOp",EDGE,"E30.bottom"),sQuery(id+"F6.wireOp",EDGE,"E30.left"),sQuery(id+"F6.wireOp",EDGE,"E30.right"),sQuery(id+"F6.wireOp",EDGE,"E32.trimOffspring"),sQuery(id+"F6.wireOp",EDGE,"E33.trimOffspring")])],"isStart":false});
            var sketch = newSketch(context, id + "F48", { "sketchPlane" : qUnion([Q0])});
            skLineSegment(sketch, "E127.bottom", {"start": v(-2.16, 23.78) * mm, "end": v(2.16, 23.78) * mm});
            skLineSegment(sketch, "E127.top", {"start": v(-2.16, 116.45) * mm, "end": v(2.16, 116.45) * mm});
            skLineSegment(sketch, "E127.left", {"start": v(-2.16, 23.78) * mm, "end": v(-2.16, 116.45) * mm});
            skLineSegment(sketch, "E127.right", {"start": v(2.16, 23.78) * mm, "end": v(2.16, 116.45) * mm});
            skSolve(sketch);
        }
        {
            var Q0;
            Q0 = qSketchRegion(id + "F48", true);
            extrude(context, id + "F49", {"entities" : qUnion([Q0]), "depth" : 1 * mm, "offsetDistance" : 25 * mm});
        }
        {
            var Q0;
            Q0=makeQuery(id+"F9.opExtrude","CAP_FACE",FACE,{"disambiguationData":[OSD([sQuery(id+"F8.wireOp",EDGE,"E34"),sQuery(id+"F8.wireOp",EDGE,"E37.MirrorCS"),sQuery(id+"F8.wireOp",EDGE,"E38.MirrorCS"),sQuery(id+"F8.wireOp",EDGE,"E40")])],"isStart":false});
            var sketch = newSketch(context, id + "F50", { "sketchPlane" : qUnion([Q0])});
            skLineSegment(sketch, "E128.bottom", {"start": v(20.38, 93.72) * mm, "end": v(28.36, 93.72) * mm});
            skLineSegment(sketch, "E128.top", {"start": v(20.38, 79.02) * mm, "end": v(28.36, 79.02) * mm});
            skLineSegment(sketch, "E128.left", {"start": v(20.38, 93.72) * mm, "end": v(20.38, 79.02) * mm});
            skLineSegment(sketch, "E128.right", {"start": v(28.36, 93.72) * mm, "end": v(28.36, 79.02) * mm});
            skSolve(sketch);
        }
        {
            var Q0;
            Q0 = qSketchRegion(id + "F50", true);
            extrude(context, id + "F51", {"entities" : qUnion([Q0]), "depth" : 10 * mm, "offsetDistance" : 25 * mm});
        }
        {
            var Q0;
            Q0=makeQuery(id+"F21.opExtrude","SWEPT_EDGE",EDGE,{"disambiguationData":[OSD([sQuery(id+"F20.wireOp",EDGE,"E107.MirrorCS"),sQuery(id+"F20.wireOp",EDGE,"E110.MirrorCS")])]});
            var Q1;
            Q1=makeQuery(id+"F21.opExtrude","SWEPT_EDGE",EDGE,{"disambiguationData":[OSD([sQuery(id+"F20.wireOp",EDGE,"E103"),sQuery(id+"F20.wireOp",EDGE,"E106")])]});
            var Q2;
            Q2=makeQuery(id+"F15.opExtrude","SWEPT_EDGE",EDGE,{"disambiguationData":[OSD([sQuery(id+"F14.wireOp",EDGE,"E64"),sQuery(id+"F14.wireOp",EDGE,"E65")])]});
            var Q3;
            Q3=makeQuery(id+"F15.opExtrude","SWEPT_EDGE",EDGE,{"disambiguationData":[OSD([sQuery(id+"F14.wireOp",EDGE,"E74.MirrorCS"),sQuery(id+"F14.wireOp",EDGE,"E80.MirrorCS")])]});
            var Q4;
            Q4=makeQuery(id+"F15.opExtrude","SWEPT_EDGE",EDGE,{"disambiguationData":[OSD([sQuery(id+"F14.wireOp",EDGE,"E65"),sQuery(id+"F14.wireOp",EDGE,"E67.trimOffspring")])]});
            var Q5;
            Q5=makeQuery(id+"F15.opExtrude","SWEPT_EDGE",EDGE,{"disambiguationData":[OSD([sQuery(id+"F14.wireOp",EDGE,"E74.MirrorCS"),sQuery(id+"F14.wireOp",EDGE,"E75.MirrorCS")])]});
            var Q6;
            Q6=makeQuery(id+"F13.opExtrude","SWEPT_EDGE",EDGE,{"disambiguationData":[OSD([sQuery(id+"F12.wireOp",EDGE,"E56"),sQuery(id+"F12.wireOp",EDGE,"E57.left")])]});
            var Q7;
            Q7=makeQuery(id+"F13.opExtrude","SWEPT_EDGE",EDGE,{"disambiguationData":[OSD([sQuery(id+"F12.wireOp",EDGE,"E57.right"),sQuery(id+"F12.wireOp",EDGE,"E58.trimOffspring")])]});
            var Q8;
            Q8=makeQuery(id+"F5.opExtrude","SWEPT_EDGE",EDGE,{"disambiguationData":[OSD([sQuery(id+"F4.wireOp",EDGE,"E22.top"),sQuery(id+"F4.wireOp",EDGE,"E22.right")])]});
            var Q9;
            Q9=makeQuery(id+"F5.opExtrude","SWEPT_EDGE",EDGE,{"disambiguationData":[OSD([sQuery(id+"F4.wireOp",EDGE,"E22.top"),sQuery(id+"F4.wireOp",EDGE,"E22.left")])]});
            fillet(context, id + "F52", {"entities" : qUnion([Q0, Q1, Q2, Q3, Q4, Q5, Q6, Q7, Q8, Q9]), "radius" : 3.2 * mm, "tangentPropagation" : true, "allowEdgeOverflow" : false});
        }
    });
